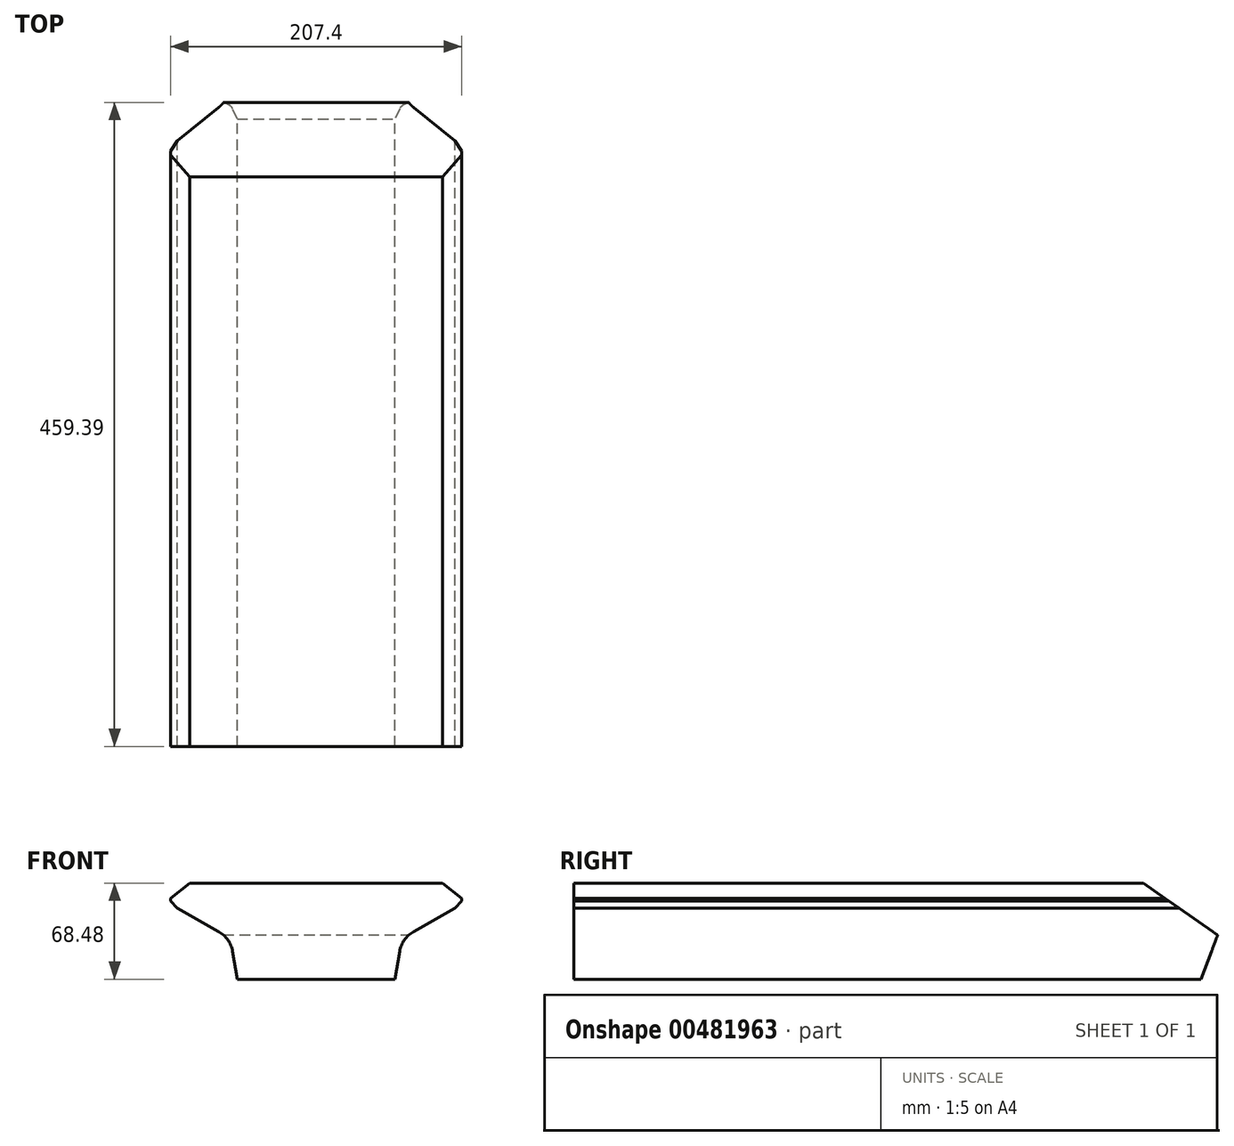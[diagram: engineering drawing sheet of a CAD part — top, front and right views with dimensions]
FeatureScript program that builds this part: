
annotation { "Feature Type Name" : "Feature", "Feature Type Description" : "" }
export const myFeature = defineFeature(function(context is Context, id is Id, definition is map)
    precondition{}
    {
        {
            var Q0;
            Q0=qCreatedBy(makeId("Front.planeOp"),FACE);
            var sketch = newSketch(context, id + "F0", { "sketchPlane" : qUnion([Q0])});
            skLineSegment(sketch, "E0", {"start": v(-56.25, 0) * mm, "end": v(56.25, 0) * mm});
            skLineSegment(sketch, "E1", {"start": v(56.25, 0) * mm, "end": v(61.18, 29.2) * mm});
            skLineSegment(sketch, "E2", {"start": v(61.18, 29.2) * mm, "end": v(-61.18, 29.2) * mm, "construction": true});
            skLineSegment(sketch, "E3", {"start": v(-61.18, 29.2) * mm, "end": v(-56.25, 0) * mm});
            skLineSegment(sketch, "E4", {"start": v(0, 0) * mm, "end": v(0, 29.2) * mm, "construction": true});
            skLineSegment(sketch, "E5", {"start": v(61.18, 29.2) * mm, "end": v(99, 50.6) * mm});
            skLineSegment(sketch, "E6", {"start": v(99, 50.6) * mm, "end": v(-99, 50.6) * mm, "construction": true});
            skLineSegment(sketch, "E7", {"start": v(-99, 50.6) * mm, "end": v(-61.18, 29.2) * mm});
            skLineSegment(sketch, "E8", {"start": v(0, 29.2) * mm, "end": v(0, 50.6) * mm, "construction": true});
            skPoint(sketch, "E8.endSnap0", {"position": v(0, 50.6) * mm});
            skLineSegment(sketch, "E9", {"start": v(-99, 50.6) * mm, "end": v(-103.7, 55.8) * mm});
            skLineSegment(sketch, "E10", {"start": v(-103.7, 55.8) * mm, "end": v(103.7, 55.8) * mm, "construction": true});
            skLineSegment(sketch, "E11", {"start": v(103.7, 55.8) * mm, "end": v(99, 50.6) * mm});
            skLineSegment(sketch, "E12", {"start": v(0, 50.6) * mm, "end": v(0, 55.8) * mm, "construction": true});
            skLineSegment(sketch, "E13", {"start": v(-103.7, 55.8) * mm, "end": v(-103.7, 57.8) * mm});
            skLineSegment(sketch, "E14", {"start": v(103.7, 55.8) * mm, "end": v(103.7, 57.8) * mm});
            skLineSegment(sketch, "E15", {"start": v(103.7, 57.8) * mm, "end": v(90.23, 68.48) * mm});
            skLineSegment(sketch, "E16", {"start": v(90.23, 68.48) * mm, "end": v(-90.23, 68.48) * mm});
            skLineSegment(sketch, "E17", {"start": v(-90.23, 68.48) * mm, "end": v(-103.7, 57.8) * mm});
            skLineSegment(sketch, "E18", {"start": v(0, 55.8) * mm, "end": v(0, 68.48) * mm, "construction": true});
            skSolve(sketch);
        }
        {
            var Q0;
            Q0 = qSketchRegion(id + "F0", true);
            extrude(context, id + "F1", {"entities" : qUnion([Q0]), "depth" : 459.4 * mm, "offsetDistance" : 25 * mm});
        }
        {
            var Q0;
            Q0=makeQuery(id+"F1.opExtrude","CAP_EDGE",EDGE,{"disambiguationData":[OSD([sQuery(id+"F0.wireOp",EDGE,"E0")])],"isStart":true});
            chamfer(context, id + "F2", {"entities" : qUnion([Q0]), "chamferType" : ChamferType.TWO_OFFSETS, "width1" : 11.8 * mm, "oppositeDirection" : false, "width2" : 31.5 * mm, "tangentPropagation" : true});
        }
        {
            var Q0;
            Q0=makeQuery(id+"F1.opExtrude","CAP_EDGE",EDGE,{"disambiguationData":[OSD([sQuery(id+"F0.wireOp",EDGE,"E16")])],"isStart":true});
            chamfer(context, id + "F3", {"entities" : qUnion([Q0]), "chamferType" : ChamferType.TWO_OFFSETS, "width1" : 52.9 * mm, "oppositeDirection" : false, "width2" : 37 * mm, "tangentPropagation" : true});
        }
        {
            var Q0;
            Q0=makeQuery(id+"F1.opExtrude","SWEPT_EDGE",EDGE,{"disambiguationData":[OSD([sQuery(id+"F0.wireOp",EDGE,"E1"),sQuery(id+"F0.wireOp",EDGE,"E5")])]});
            var Q1;
            Q1=makeQuery(id+"F1.opExtrude","SWEPT_EDGE",EDGE,{"disambiguationData":[OSD([sQuery(id+"F0.wireOp",EDGE,"E3"),sQuery(id+"F0.wireOp",EDGE,"E7")])]});
            fillet(context, id + "F4", {"entities" : qUnion([Q0, Q1]), "tangentPropagation" : true, "radius" : 20 * mm, "defaultsChanged" : true, "vertexSettings" : [], "allowEdgeOverflow" : false});
        }
    });
